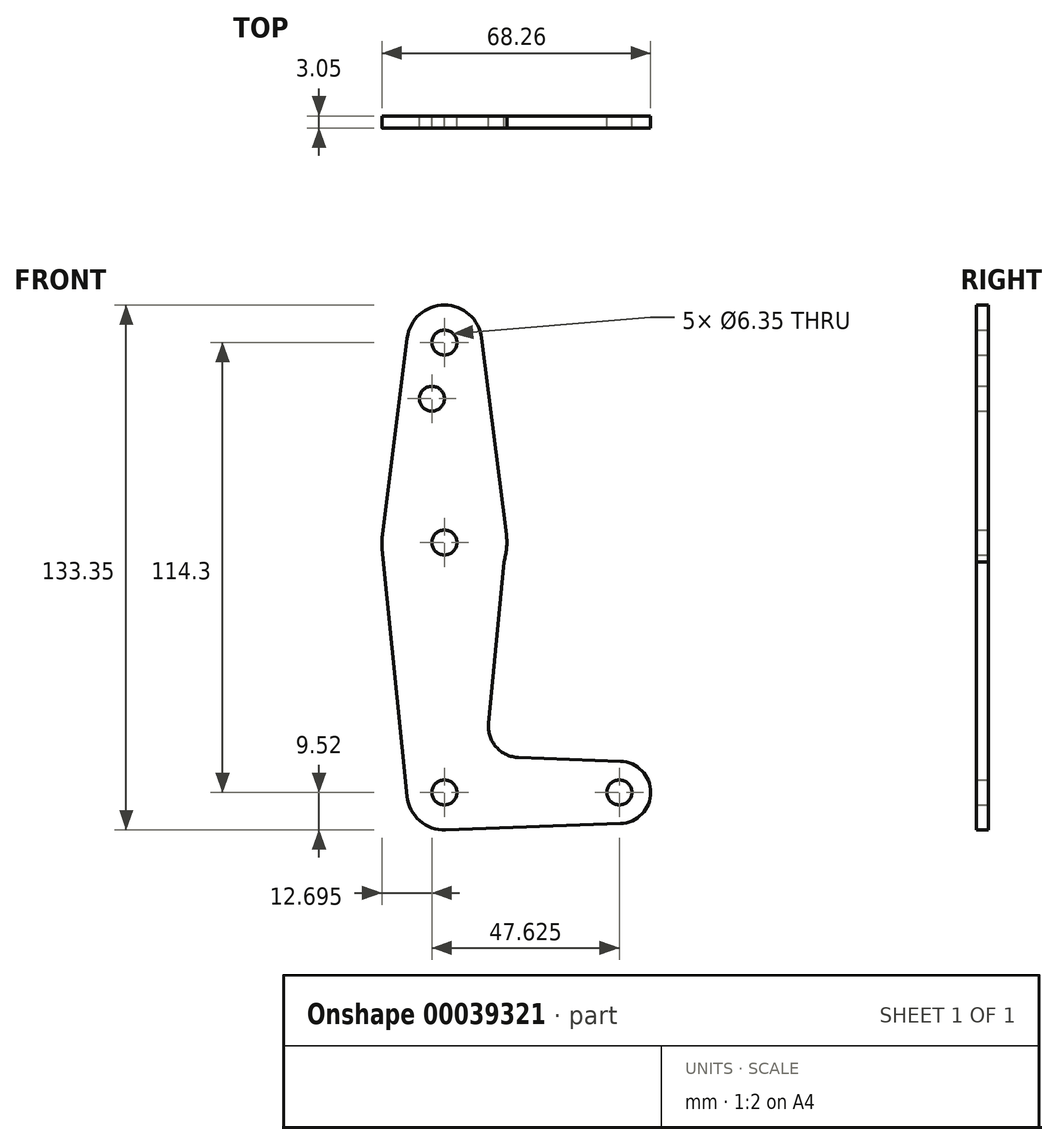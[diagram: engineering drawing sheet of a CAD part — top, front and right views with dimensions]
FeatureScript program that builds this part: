
annotation { "Feature Type Name" : "Feature", "Feature Type Description" : "" }
export const myFeature = defineFeature(function(context is Context, id is Id, definition is map)
    precondition{}
    {
        {
            var Q0;
            Q0=qCreatedBy(makeId("Front.planeOp"),FACE);
            var sketch = newSketch(context, id + "F0", { "sketchPlane" : qUnion([Q0])});
            skLineSegment(sketch, "E0", {"start": v(0, 0) * mm, "end": v(0, 63.5) * mm, "construction": true});
            skLineSegment(sketch, "E1", {"start": v(0, 63.5) * mm, "end": v(0, 114.3) * mm, "construction": true});
            skLineSegment(sketch, "E2", {"start": v(0, 0) * mm, "end": v(44.45, 0) * mm, "construction": true});
            skCircle(sketch, "E3", {"center": v(0, 114.3) * mm, "radius": 9.53 * mm});
            skCircle(sketch, "E4", {"center": v(0, 63.5) * mm, "radius": 15.88 * mm});
            skCircle(sketch, "E5", {"center": v(0, 0) * mm, "radius": 9.53 * mm});
            skCircle(sketch, "E6", {"center": v(44.45, 0) * mm, "radius": 7.94 * mm});
            skLineSegment(sketch, "E7", {"start": v(-9.45, 115.5) * mm, "end": v(-15.75, 65.48) * mm});
            skLineSegment(sketch, "E8", {"start": v(9.45, 115.5) * mm, "end": v(15.75, 65.48) * mm});
            skLineSegment(sketch, "E9", {"start": v(15.75, 65.48) * mm, "end": v(11.22, 17.55) * mm});
            skLineSegment(sketch, "E10", {"start": v(18.86, 8.86) * mm, "end": v(44.73, 7.93) * mm});
            skCircle(sketch, "E11", {"center": v(0, 114.3) * mm, "radius": 3.18 * mm});
            skCircle(sketch, "E12", {"center": v(-3.18, 100.03) * mm, "radius": 3.18 * mm});
            skCircle(sketch, "E13", {"center": v(0, 63.5) * mm, "radius": 3.18 * mm});
            skCircle(sketch, "E14", {"center": v(0, 0) * mm, "radius": 3.18 * mm});
            skCircle(sketch, "E15", {"center": v(44.45, 0) * mm, "radius": 3.18 * mm});
            skPoint(sketch, "E16.newPointB", {"position": v(0, 9.53) * mm});
            skArc(sketch, "E16.filletArc", {"start": v(11.22, 17.55) * mm, "mid": v(13.16, 11.56) * mm, "end": v(18.86, 8.86) * mm});
            skLineSegment(sketch, "E17", {"start": v(0.34, -9.52) * mm, "end": v(44.73, -7.93) * mm});
            skLineSegment(sketch, "E18", {"start": v(-15.8, 61.91) * mm, "end": v(-9.48, -0.95) * mm});
            skSolve(sketch);
        }
        {
            var Q0;
            Q0 = qSketchRegion(id + "F0", true);
            extrude(context, id + "F1", {"entities" : qUnion([Q0]), "depth" : 3.05 * mm});
        }
    });
